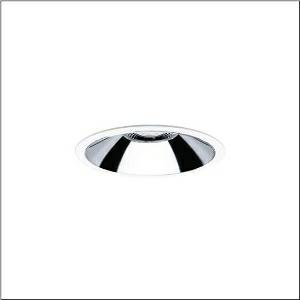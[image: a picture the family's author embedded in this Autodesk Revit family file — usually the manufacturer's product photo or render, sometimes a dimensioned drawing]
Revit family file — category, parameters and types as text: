
# Revit family: lunis_21_xl_51db15mf4d
name_source: partatom
category: Lighting Fixtures
units: mm (PartAtom-declared; Revit-internal decimal feet)

## family parameters
Cut with Voids When Loaded = No
Host = Face
Light Source = No
Part Type = Normal
Room Calculation Point = No
Round Connector Dimension = Use Diameter
Shared = No

## types (1)
- --- (1 x LED, 3000 lm, 24.3 W, 4000K)
    Apparent Load = 24 VA
    CIE Flux Codes = 89 99 100 100 100
    Color Rendering = 80
    Color Temperature = 4000K
    Default Elevation = 1800 mm
    Description = Lunis 21,  XL, downlight, of PC, light emission: direct distribution, LED rated luminous flux: 2.280lm, light colour: 840, control gear: ECG, with terminal, 3-pole, mains connection: 220..240V, AC, housing, round, of diecast aluminium, traffic white (RAL 9016), diameter: 213mm, protection rating (complete): IP20, protection rating (on room side): IP54, insulation class (complete): insulation class II (safety insulation), certification: CE, impact resistance: IK02, packaging unit: 1 piece
    Height = 0 mm  [stored 0 ft]
    Lamp = 1 x LED
    Lamp Light Flux = 3000 lm
    Lamp Power = 24.3 W
    Lamp count = 1
    Length = 213 mm
    Luminous efficacy = 123 lm/W
    Manufacturer = Siteco
    ModVariant = No
    Model = 51DB15MF4D
    Mounting Place = Ceiling
    Mounting Type = Recessed
    Number of Poles = 1
    OnlyDefault = Yes
    Power Factor = 1
    Product Name = Lunis 21 XL
    Product group = downlight
    ProductGroupID = 400
    Protection Class = Protection class II
    Protection Degree = IP 20
    RLX_Detail_Level = 1
    RLX_Emergency_Light_Flux = 0 lm
    RLX_Emergency_Type = 0
    RLX_Emergency_Type_DB = No
    RlxData = <blob elided: 27581 chars, md5=9c4acb15>
    Socket = socket
    Standby Power = 0 W
    System Light Flux = 3000 lm
    System Power = 24 W
    Type Comments = factory setting: luminous flux: 100 % | (ON | ON)
    Type Image = l_1287385.jpg
    URL = http://relux.com
    VarID = @adj_150928
    Voltage = 0 V
    Weight = 0.00 kg
    Width = 0 mm  [stored 0 ft]

note: [stored X ft] marks values corroborated as IEEE doubles in the binary element streams (Revit-internal decimal feet)

## geometry (parser evidence)
native form markers: Blend x4, Sweep x11
no freeform markers — native parametric forms only
